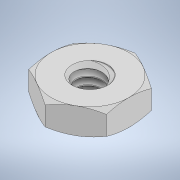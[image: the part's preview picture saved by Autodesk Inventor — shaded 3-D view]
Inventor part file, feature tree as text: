
AUTODESK INVENTOR PART (.ipt)
format: ipt  version: 2021 (Build 250183000, 183)  size: 258,048 bytes
history: native  units: in
note: dims shown in document units (in); Inventor stores cm internally (conversion verified against a paired STEP export)
features: mirror x1
ambient origin geometry x8: Origin, YZ Plane, XZ Plane, XY Plane, X Axis, Y Axis, Z Axis, Center Point
bodies: Solid1 (feature_tree)
feature tree (1):
  mirror  "Mirror1"
